# Revit family: ADB Electric grills cupboard 410
name_source: partatom
category: Equipement spécialisé
units: mm (PartAtom-declared; Revit-internal decimal feet)

## family parameters
Basée sur le plan de construction = Non
Conserver l'orientation des annotations = Non
Cote de connecteur circulaire = Utiliser le diamètre
Couper avec des vides une fois chargée = Non
Numéro OmniClass = 23.40.40.14.17.11
Partagée = Non
Repère de localisation dans la pièce = Non
Titre OmniClass = Cookers, Ovens, Stoves
Toujours verticalement = Oui
Type d'élément = Normal

## types (4) — shared parameters
C = 200 mm  [stored 0.656168 ft]
Commentaires du type = Ambassade range - Electric grills & plancha
D = 740 mm  [stored 2.42782 ft]
Fabricant = Société Industrielle de Lacanche
URL = https://www.ambassade-de-bourgogne.com
URL Cutsheet = https://www.ambassade-de-bourgogne.com
zero-valued in all types: Elévation par défaut

## per-type parameters (varying)
| type | Description | Height | Table |
| CME 410 GR | Ridged cast iron electric grill cupboard | 1015 mm  [stored 3.33005 ft] | CME410 GR_GL_gril électrique : GR |
| CME 410 GL | Smooth cast iron electric grill cupboard | 1015 mm  [stored 3.33005 ft] | CME410 GR_GL_gril électrique : GL |
| CME 410 SLK | Smooth steel electric grill cupboard | 990 mm  [stored 3.24803 ft] | CME410 SLK_SLKC_gril électrique : SLK |
| CME 410 SLKC | Smooth chrome electric grill cupboard | 990 mm  [stored 3.24803 ft] | CME410 SLK_SLKC_gril électrique : SLKC |

note: column(s) folded — value = type name in every type: Modèle

note: [stored X ft] marks values corroborated as IEEE doubles in the binary element streams (Revit-internal decimal feet)
